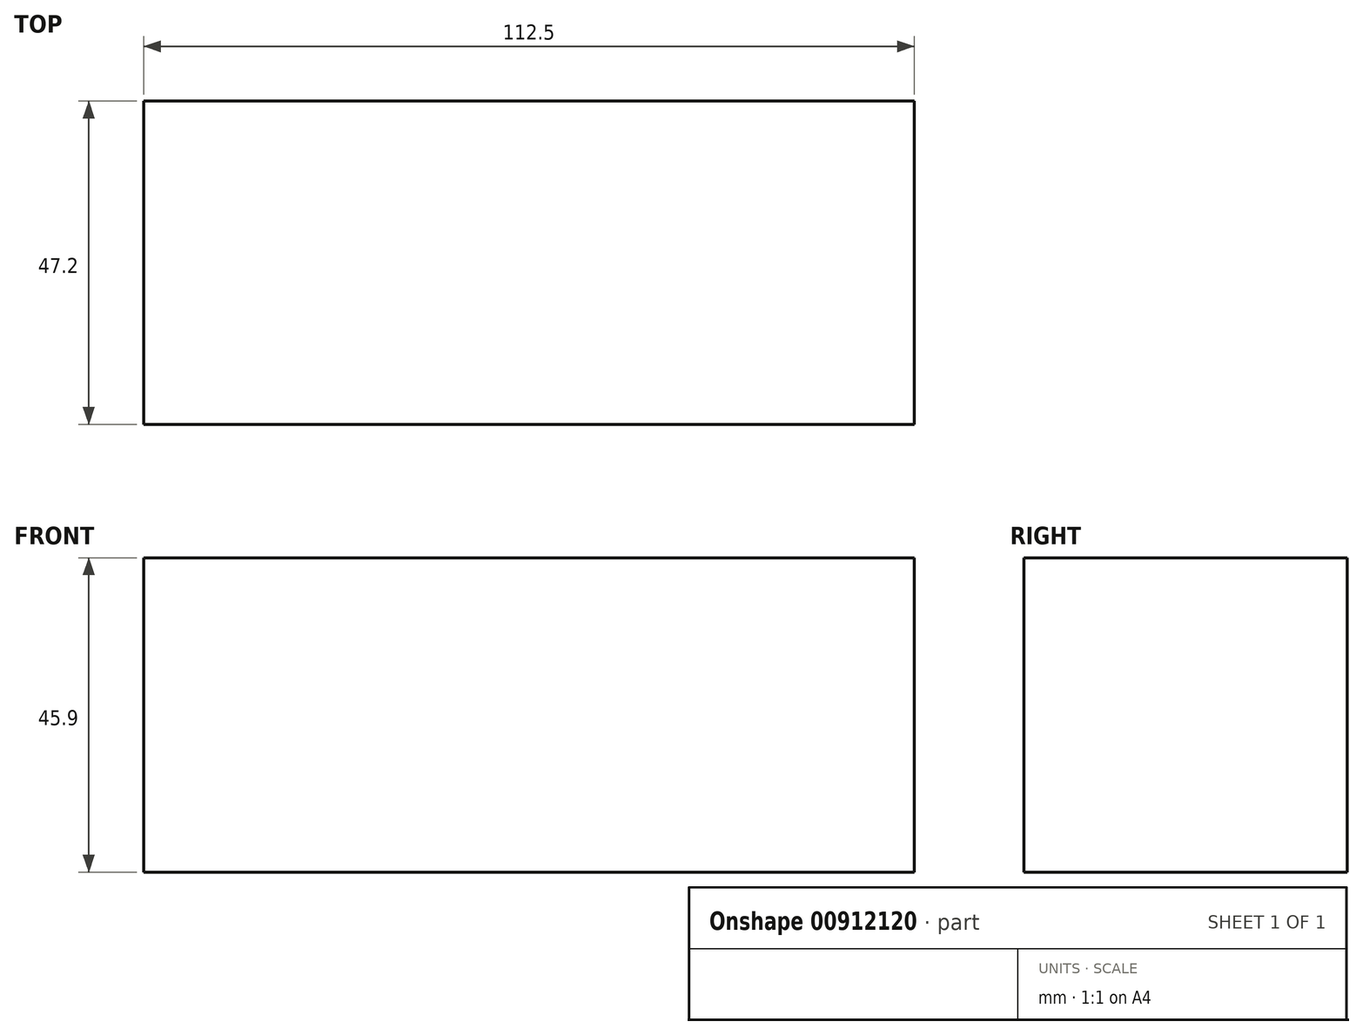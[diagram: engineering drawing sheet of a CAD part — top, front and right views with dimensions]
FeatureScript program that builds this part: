
annotation { "Feature Type Name" : "Feature", "Feature Type Description" : "" }
export const myFeature = defineFeature(function(context is Context, id is Id, definition is map)
    precondition{}
    {
        {
            var Q0;
            Q0=qCreatedBy(makeId("Front.planeOp"),FACE);
            var sketch = newSketch(context, id + "F0", { "sketchPlane" : qUnion([Q0])});
            skLineSegment(sketch, "E0.bottom", {"start": v(56.25, -23.78) * mm, "end": v(-56.25, -23.78) * mm});
            skLineSegment(sketch, "E0.top", {"start": v(56.25, 22.12) * mm, "end": v(-56.25, 22.12) * mm});
            skLineSegment(sketch, "E0.left", {"start": v(56.25, -23.78) * mm, "end": v(56.25, 22.12) * mm});
            skLineSegment(sketch, "E0.right", {"start": v(-56.25, -23.78) * mm, "end": v(-56.25, 22.12) * mm});
            skPoint(sketch, "E0.middle", {"position": v(0, -0.83) * mm});
            skSolve(sketch);
        }
        {
            var Q0;
            Q0=makeQuery(id+"F0.imprint","IMPRINT",FACE,{"disambiguationData":[TD([[makeQuery(id+"F0.imprint","IMPRINT",EDGE,{"derivedFrom":sQuery(id+"F0.wireOp",EDGE,"E0.bottom")}),-1.0]])]});
            extrude(context, id + "F1", {"entities" : qUnion([Q0]), "depth" : 47.2 * mm, "offsetDistance" : 25.4 * mm});
        }
    });
